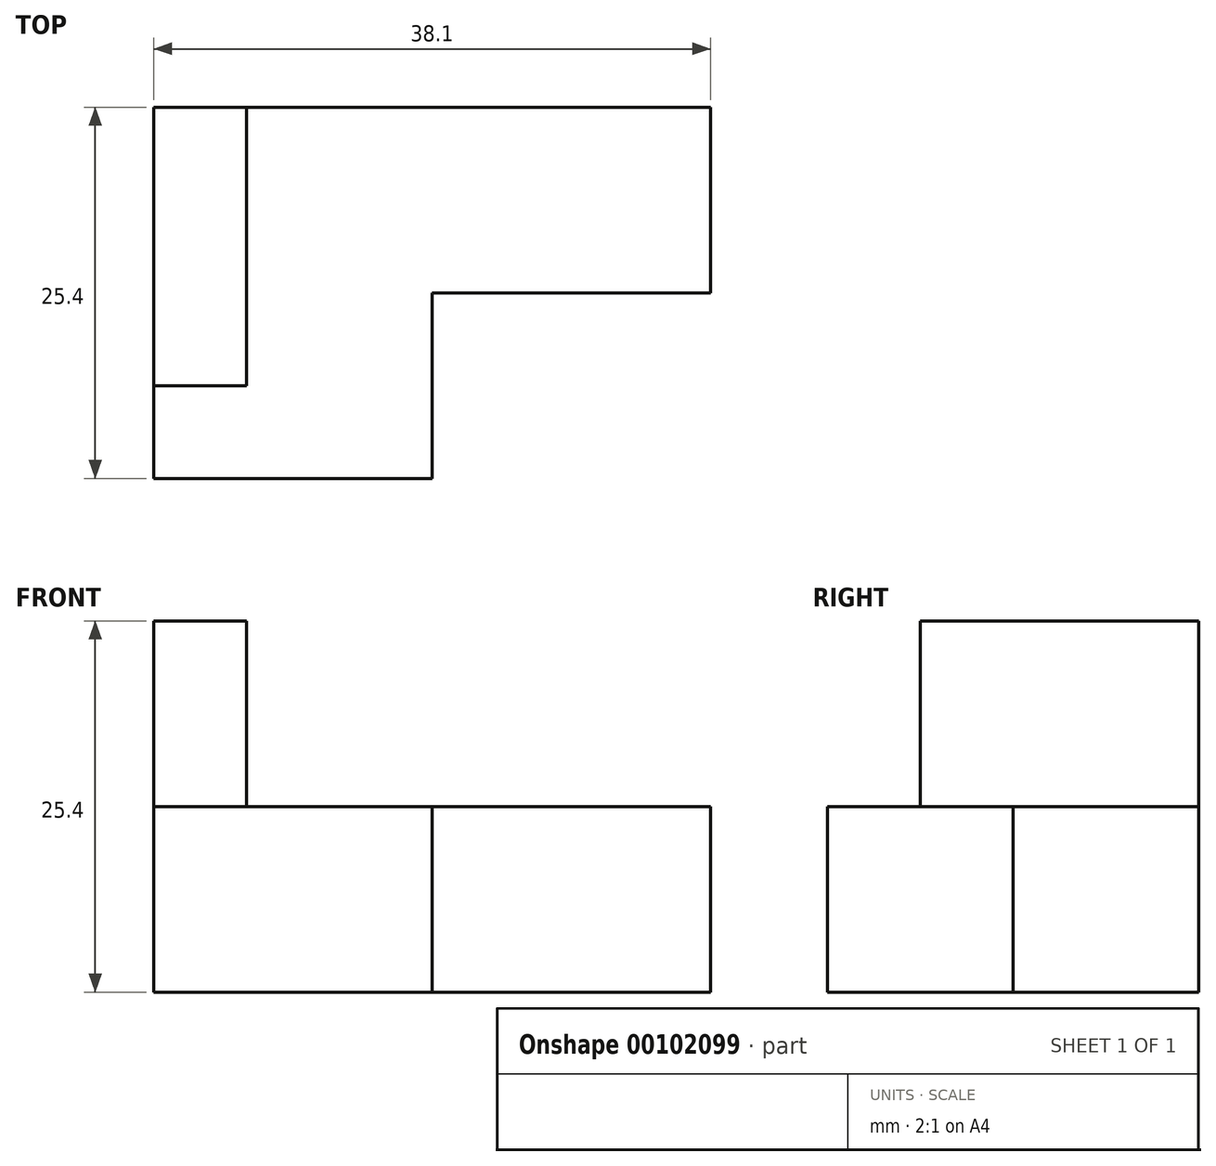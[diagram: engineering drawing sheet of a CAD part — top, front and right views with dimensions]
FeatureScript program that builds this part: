
annotation { "Feature Type Name" : "Feature", "Feature Type Description" : "" }
export const myFeature = defineFeature(function(context is Context, id is Id, definition is map)
    precondition{}
    {
        {
            var Q0;
            Q0=qCreatedBy(makeId("Front.planeOp"),FACE);
            var sketch = newSketch(context, id + "F0", { "sketchPlane" : qUnion([Q0])});
            skLineSegment(sketch, "E0", {"start": v(-31.75, 0) * mm, "end": v(0, 0) * mm});
            skLineSegment(sketch, "E1", {"start": v(-31.75, 0) * mm, "end": v(-31.75, 12.7) * mm});
            skLineSegment(sketch, "E2", {"start": v(-31.75, 12.7) * mm, "end": v(-38.1, 12.7) * mm});
            skLineSegment(sketch, "E3", {"start": v(-38.1, 12.7) * mm, "end": v(-38.1, -12.7) * mm});
            skLineSegment(sketch, "E4", {"start": v(0, -12.7) * mm, "end": v(0, 0) * mm});
            skLineSegment(sketch, "E5", {"start": v(-38.1, -12.7) * mm, "end": v(0, -12.7) * mm});
            skSolve(sketch);
        }
        {
            var Q0;
            Q0 = qSketchRegion(id + "F0", true);
            extrude(context, id + "F1", {"entities" : qUnion([Q0]), "depth" : 25.4 * mm});
        }
        {
            var Q0;
            Q0=qCreatedBy(makeId("Right.planeOp"),FACE);
            var sketch = newSketch(context, id + "F2", { "sketchPlane" : qUnion([Q0])});
            skLineSegment(sketch, "E6.bottom", {"start": v(-19.05, 0) * mm, "end": v(-25.4, 0) * mm});
            skLineSegment(sketch, "E6.top", {"start": v(-19.05, 12.7) * mm, "end": v(-25.4, 12.7) * mm});
            skLineSegment(sketch, "E6.left", {"start": v(-19.05, 0) * mm, "end": v(-19.05, 12.7) * mm});
            skLineSegment(sketch, "E6.right", {"start": v(-25.4, 0) * mm, "end": v(-25.4, 12.7) * mm});
            skSolve(sketch);
        }
        {
            var Q0;
            Q0 = qSketchRegion(id + "F2", true);
            extrude(context, id + "F3", {"entities" : qUnion([Q0]), "operationType" : NewBodyOperationType.REMOVE, "endBound" : BoundingType.THROUGH_ALL, "oppositeDirection" : true, "depth" : 38.1 * mm});
        }
        {
            var Q0;
            Q0=qCreatedBy(makeId("Right.planeOp"),FACE);
            var sketch = newSketch(context, id + "F4", { "sketchPlane" : qUnion([Q0])});
            skLineSegment(sketch, "E7.bottom", {"start": v(-25.4, 0) * mm, "end": v(-12.7, 0) * mm});
            skLineSegment(sketch, "E7.top", {"start": v(-25.4, -12.7) * mm, "end": v(-12.7, -12.7) * mm});
            skLineSegment(sketch, "E7.left", {"start": v(-25.4, 0) * mm, "end": v(-25.4, -12.7) * mm});
            skLineSegment(sketch, "E7.right", {"start": v(-12.7, 0) * mm, "end": v(-12.7, -12.7) * mm});
            skSolve(sketch);
        }
        {
            var Q0;
            Q0 = qSketchRegion(id + "F4", true);
            extrude(context, id + "F5", {"entities" : qUnion([Q0]), "operationType" : NewBodyOperationType.REMOVE, "oppositeDirection" : true, "depth" : 19.05 * mm});
        }
    });
